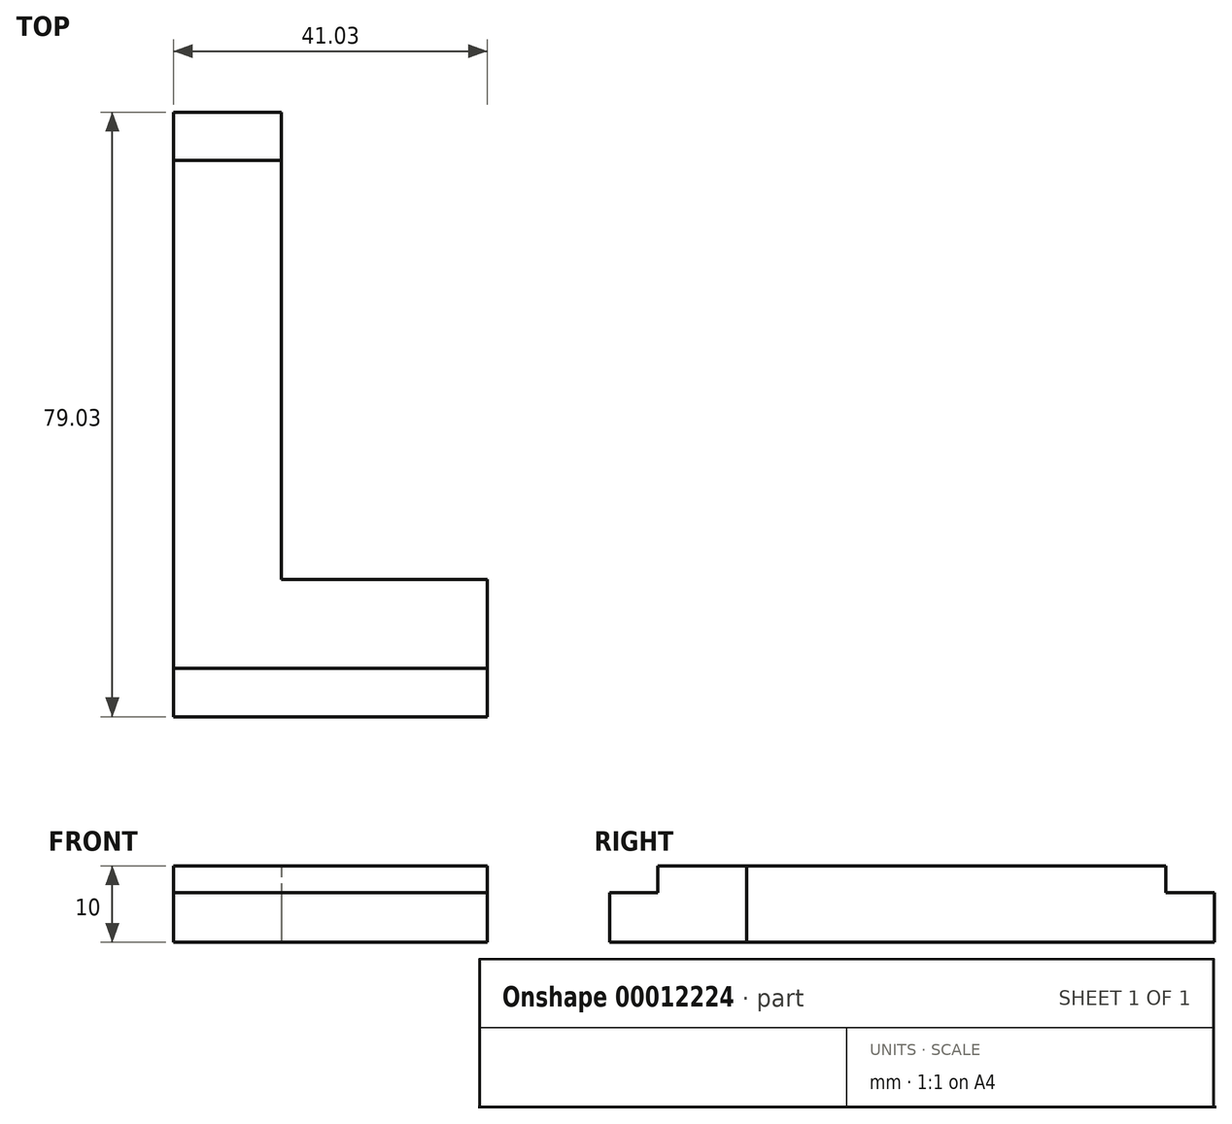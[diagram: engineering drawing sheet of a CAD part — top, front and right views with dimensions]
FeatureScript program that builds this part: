
annotation { "Feature Type Name" : "Feature", "Feature Type Description" : "" }
export const myFeature = defineFeature(function(context is Context, id is Id, definition is map)
    precondition{}
    {
        {
            var Q0;
            Q0=qCreatedBy(makeId("Top.planeOp"),FACE);
            var sketch = newSketch(context, id + "F0", { "sketchPlane" : qUnion([Q0])});
            skText(sketch, "E0", { "text": "L", "fontName": "OpenSans-Bold.ttf"});
            const initialGuessF0  = {"E0": [-0.0494, 0, 1, 0, 0.067]};
            skSetInitialGuess(sketch, initialGuessF0);
            skSolve(sketch);
        }
        {
            var Q0;
            Q0=makeQuery(id+"F0.imprint","IMPRINT",FACE,{"disambiguationData":[TD([[makeQuery(id+"F0.imprint","IMPRINT",EDGE,{"derivedFrom":sQuery(id+"F0.wireOp",EDGE,"E0.sketch_text.stroke-0")}),-1.0]])]});
            extrude(context, id + "F1", {"entities" : qUnion([Q0]), "depth" : 10 * mm});
        }
        {
            var Q0;
            Q0=makeQuery(id+"F1.opExtrude","SWEPT_FACE",FACE,{"disambiguationData":[OSD([sQuery(id+"F0.wireOp",EDGE,"E0.sketch_text.stroke-5")])]});
            var sketch = newSketch(context, id + "F2", { "sketchPlane" : qUnion([Q0])});
            skLineSegment(sketch, "E1.0.0", {"start": v(-41.03, 0) * mm, "end": v(0, 0) * mm});
            skLineSegment(sketch, "E1.0.1", {"start": v(0, 0) * mm, "end": v(0, 10) * mm});
            skLineSegment(sketch, "E1.0.2", {"start": v(0, 10) * mm, "end": v(-41.03, 10) * mm});
            skLineSegment(sketch, "E1.0.3", {"start": v(-41.03, 10) * mm, "end": v(-41.03, 0) * mm});
            skLineSegment(sketch, "E2.top", {"start": v(-41.03, 6.5) * mm, "end": v(0, 6.5) * mm});
            skLineSegment(sketch, "E2.left", {"start": v(-41.03, 0) * mm, "end": v(-41.03, 6.5) * mm});
            skLineSegment(sketch, "E2.right", {"start": v(0, 0) * mm, "end": v(0, 6.5) * mm});
            skSolve(sketch);
        }
        {
            var Q0;
            Q0=makeQuery(id+"F2.imprint","IMPRINT",FACE,{"disambiguationData":[TD([[makeQuery(id+"F2.imprint","IMPRINT",EDGE,{"derivedFrom":sQuery(id+"F2.wireOp",EDGE,"E1.0.0")}),-1.0]])]});
            extrude(context, id + "F3", {"entities" : qUnion([Q0]), "operationType" : NewBodyOperationType.ADD, "depth" : 6.3 * mm});
        }
        {
            var Q0;
            Q0=makeQuery(id+"F1.opExtrude","SWEPT_FACE",FACE,{"disambiguationData":[OSD([sQuery(id+"F0.wireOp",EDGE,"E0.sketch_text.stroke-1")])]});
            var sketch = newSketch(context, id + "F4", { "sketchPlane" : qUnion([Q0])});
            skLineSegment(sketch, "E3.0.0", {"start": v(26.94, 0) * mm, "end": v(41.03, 0) * mm});
            skLineSegment(sketch, "E3.0.1", {"start": v(41.03, 0) * mm, "end": v(41.03, 10) * mm});
            skLineSegment(sketch, "E3.0.2", {"start": v(41.03, 10) * mm, "end": v(26.94, 10) * mm});
            skLineSegment(sketch, "E3.0.3", {"start": v(26.94, 10) * mm, "end": v(26.94, 0) * mm});
            skLineSegment(sketch, "E4.top", {"start": v(26.94, 6.5) * mm, "end": v(41.03, 6.5) * mm});
            skLineSegment(sketch, "E4.left", {"start": v(26.94, 0) * mm, "end": v(26.94, 6.5) * mm});
            skLineSegment(sketch, "E4.right", {"start": v(41.03, 0) * mm, "end": v(41.03, 6.5) * mm});
            skSolve(sketch);
        }
        {
            var Q0;
            Q0=makeQuery(id+"F4.imprint","IMPRINT",FACE,{"disambiguationData":[TD([[makeQuery(id+"F4.imprint","IMPRINT",EDGE,{"derivedFrom":sQuery(id+"F4.wireOp",EDGE,"E3.0.0")}),-1.0]])]});
            extrude(context, id + "F5", {"entities" : qUnion([Q0]), "operationType" : NewBodyOperationType.ADD, "depth" : 6.3 * mm});
        }
    });
